# Revit family: HY-6000
name_source: partatom
category: Plumbing Fixtures
units: mm (PartAtom-declared; Revit-internal decimal feet)

## family parameters
Classification Number = 23.45.55.21
Cut with Voids When Loaded = No
Enable Cutting in Views = No
Host = Face
Maintain Annotation Orientation = No
Part Type = Normal
Room Calculation Point = No
Round Connector Dimension = Use Diameter
Shared = No

## types (10) — shared parameters
Hydrant Material = Chrome Plated
Manufacturer = MIFAB
Model = MHY-60
zero-valued in all types: Default Elevation, WFU

## per-type parameters (varying)
| type | Bury Depth | Description | URL |
| MHY-60-1 | 12 " | Lawn / Ground Hydrant | www.mifab.com |
| MHY-60-2 | 24 " | LAWN / GROUND HYDRANT | WWW.MIFAB.COM |
| MHY-60-3 | 36 " | LAWN / GROUND HYDRANT | WWW.MIFAB.COM |
| MHY-60-4 | 48 " | LAWN / GROUND HYDRANT | WWW.MIFAB.COM |
| MHY-60-5 | 60 " | LAWN / GROUND HYDRANT | WWW.MIFAB.COM |
| MHY-60-6 | 72 " | LAWN / GROUND HYDRANT | WWW.MIFAB.COM |
| MHY-60-7 | 84 " | LAWN / GROUND HYDRANT | WWW.MIFAB.COM |
| MHY-60-8 | 96 " | LAWN / GROUND HYDRANT | WWW.MIFAB.COM |
| MHY-60-9 | 108 " | LAWN / GROUND HYDRANT | WWW.MIFAB.COM |
| MHY-60-10 | 120 " | LAWN / GROUND HYDRANT | WWW.MIFAB.COM |

## geometry (parser evidence)
native form markers: Blend x2, Sweep x3
no freeform markers — native parametric forms only
